FCSTD DOCUMENT  (FreeCAD 0.20R29603 (Git))
Label: seat_side_support
License: Creative Commons Attribution
LicenseURL: http://creativecommons.org/licenses/by/4.0/
objects: Sketcher::SketchObject×1, PartDesign::Body×1
note: 2 computed .brp shape members not serialized (recipe doc carries the construction recipe); baked Part::Feature solids carry a one-line shape summary decoded from their .brp

FEATURE [Sketcher::SketchObject] Sketch001
  FullyConstrained = false
  MapMode = 5
  Placement = pos=(0,0,0) rot=(1,0,0;1.5708rad)
  Support = -> [XZ_Plane]
  sketch-geometry (6):
    g0: LineSegment StartX=-529.126 StartY=71.7895 StartZ=0 EndX=-533.553 EndY=21.1828 EndZ=0
    g1: LineSegment StartX=-533.553 StartY=21.1828 StartZ=0 EndX=529.126 EndY=-71.7895 EndZ=0
    g2: LineSegment StartX=529.126 StartY=-71.7895 StartZ=0 EndX=533.553 EndY=-21.1828 EndZ=0
    g3: LineSegment StartX=533.553 StartY=-21.1828 StartZ=0 EndX=-529.126 EndY=71.7895 EndZ=0
    g4: GeomPoint X=0 Y=0 Z=0
    g5: LineSegment StartX=-533.553 StartY=21.1828 StartZ=0 EndX=-483.139 EndY=16.7722 EndZ=0
  constraints (13):
    c: Coincident(g0,g1)
    c: Coincident(g1,g2)
    c: Coincident(g2,g3)
    c: Coincident(g3,g0)
    c: Symmetric(g1,g0,g4)
    c: Parallel(g3,g1)
    c: Parallel(g2,g0)
    c: Coincident(g4,g-1)
    c: Distance(g2) = 50.8
    c: Perpendicular(g2,g3)
    c: Angle(g3,g-1) = 0.0872665
    c: Tangent(g5,g1)
    c: Distance(g3) = 1066.74
FEATURE [PartDesign::Body] Body
  Group = -> [Sketch001]
  Origin = -> Origin
